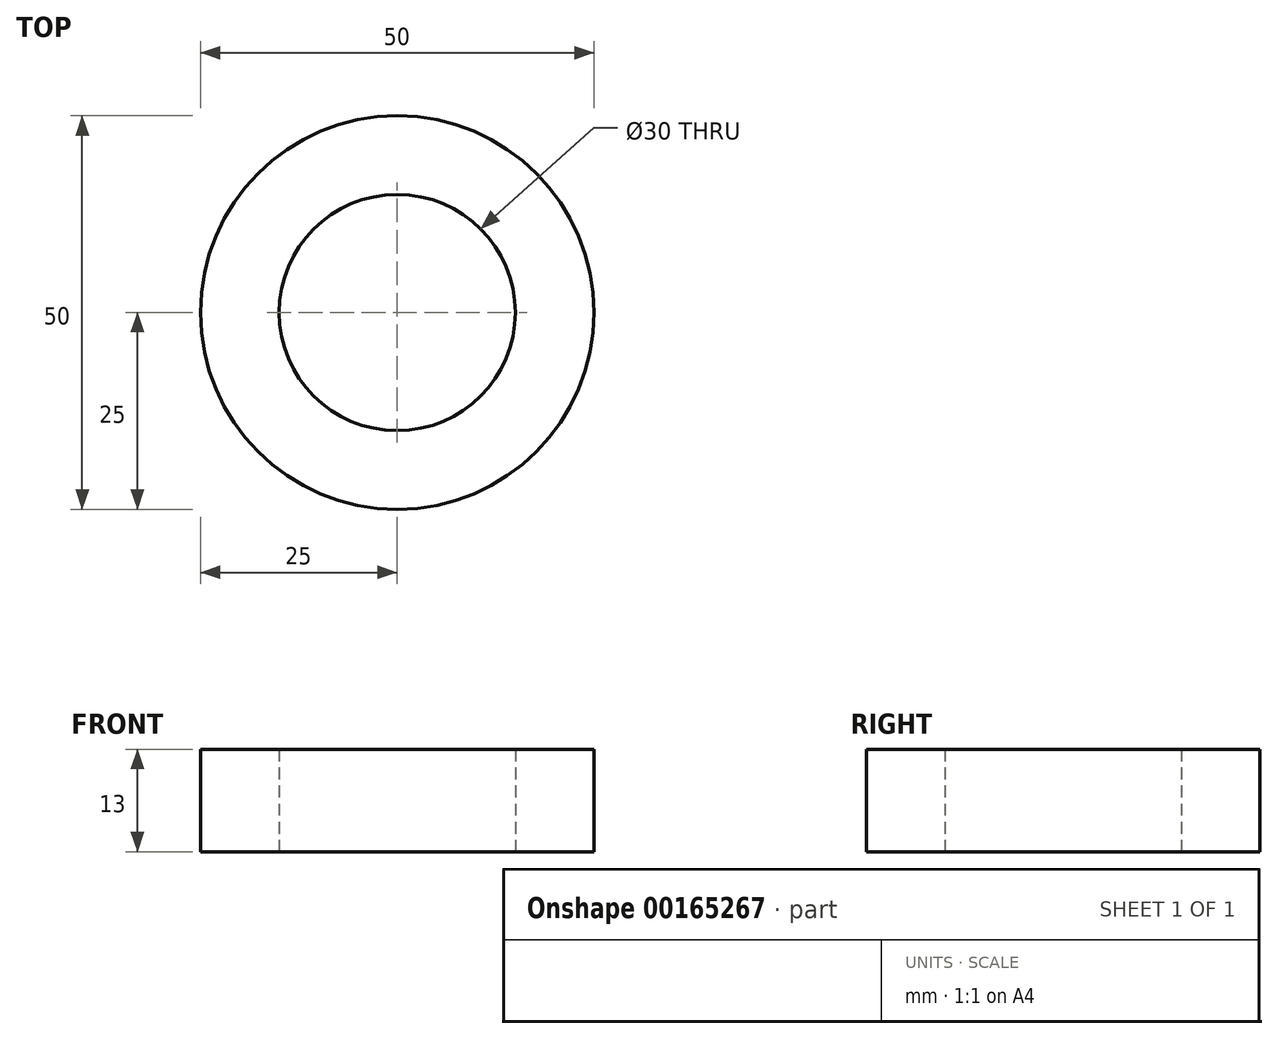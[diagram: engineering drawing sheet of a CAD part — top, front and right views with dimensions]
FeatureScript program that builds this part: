
annotation { "Feature Type Name" : "Feature", "Feature Type Description" : "" }
export const myFeature = defineFeature(function(context is Context, id is Id, definition is map)
    precondition{}
    {
        {
            var Q0;
            Q0=qCreatedBy(makeId("Top.planeOp"),FACE);
            var sketch = newSketch(context, id + "F0", { "sketchPlane" : qUnion([Q0])});
            skCircle(sketch, "E0", {"center": v(0, 0) * mm, "radius": 25 * mm});
            skCircle(sketch, "E1", {"center": v(0, 0) * mm, "radius": 15 * mm});
            skSolve(sketch);
        }
        {
            var Q0;
            Q0=makeQuery(id+"F0.imprint","IMPRINT",FACE,{"disambiguationData":[TD([[makeQuery(id+"F0.imprint","IMPRINT",EDGE,{"derivedFrom":sQuery(id+"F0.wireOp",EDGE,"E0")}),1.0]])]});
            extrude(context, id + "F1", {"entities" : qUnion([Q0]), "depth" : 13 * mm});
        }
    });
